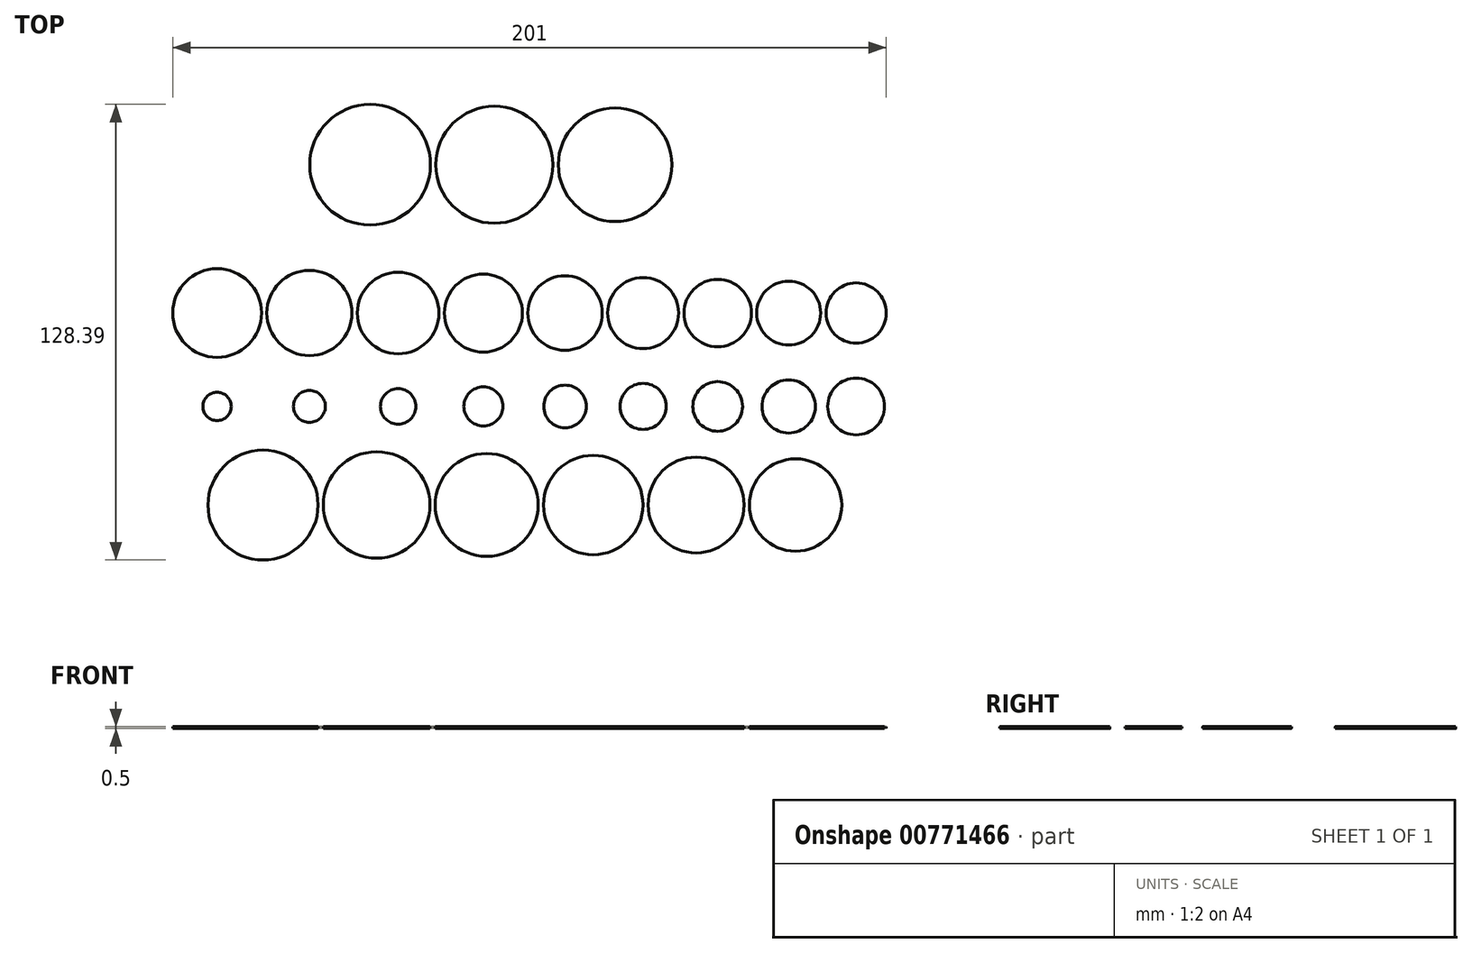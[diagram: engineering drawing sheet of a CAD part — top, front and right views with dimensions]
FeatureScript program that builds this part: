
annotation { "Feature Type Name" : "Feature", "Feature Type Description" : "" }
export const myFeature = defineFeature(function(context is Context, id is Id, definition is map)
    precondition{}
    {
        {
            var Q0;
            Q0=qCreatedBy(makeId("Top.planeOp"),FACE);
            var sketch = newSketch(context, id + "F0", { "sketchPlane" : qUnion([Q0])});
            skLineSegment(sketch, "E0", {"start": v(-97.7, 0) * mm, "end": v(119.62, 0) * mm, "construction": true});
            skCircle(sketch, "E1", {"center": v(-89.8, 0) * mm, "radius": 12.5 * mm});
            skCircle(sketch, "E2", {"center": v(-63.8, 0) * mm, "radius": 12 * mm});
            skCircle(sketch, "E3", {"center": v(-38.8, 0) * mm, "radius": 11.5 * mm});
            skCircle(sketch, "E4", {"center": v(-14.8, 0) * mm, "radius": 11 * mm});
            skCircle(sketch, "E5", {"center": v(8.2, 0) * mm, "radius": 10.5 * mm});
            skCircle(sketch, "E6", {"center": v(30.2, 0) * mm, "radius": 10 * mm});
            skCircle(sketch, "E7", {"center": v(51.2, 0) * mm, "radius": 9.5 * mm});
            skCircle(sketch, "E8", {"center": v(71.2, 0) * mm, "radius": 9 * mm});
            skCircle(sketch, "E9", {"center": v(90.2, 0) * mm, "radius": 8.5 * mm});
            skLineSegment(sketch, "E10", {"start": v(-97.7, -26.31) * mm, "end": v(119.62, -26.31) * mm, "construction": true});
            skCircle(sketch, "E11", {"center": v(-89.8, -26.31) * mm, "radius": 4 * mm});
            skCircle(sketch, "E12", {"center": v(-63.8, -26.31) * mm, "radius": 4.5 * mm});
            skCircle(sketch, "E13", {"center": v(-38.8, -26.31) * mm, "radius": 5 * mm});
            skCircle(sketch, "E14", {"center": v(-14.8, -26.31) * mm, "radius": 5.5 * mm});
            skCircle(sketch, "E15", {"center": v(8.2, -26.31) * mm, "radius": 6 * mm});
            skCircle(sketch, "E16", {"center": v(30.2, -26.31) * mm, "radius": 6.5 * mm});
            skCircle(sketch, "E17", {"center": v(51.2, -26.31) * mm, "radius": 7 * mm});
            skCircle(sketch, "E18", {"center": v(71.2, -26.31) * mm, "radius": 7.5 * mm});
            skCircle(sketch, "E19", {"center": v(90.2, -26.31) * mm, "radius": 8 * mm});
            skLineSegment(sketch, "E20", {"start": v(-97.7, -54.09) * mm, "end": v(120.28, -54.09) * mm, "construction": true});
            skCircle(sketch, "E21", {"center": v(-46.7, 41.8) * mm, "radius": 17 * mm});
            skCircle(sketch, "E22", {"center": v(-11.7, 41.8) * mm, "radius": 16.5 * mm});
            skCircle(sketch, "E23", {"center": v(22.3, 41.8) * mm, "radius": 16 * mm});
            skCircle(sketch, "E24", {"center": v(-76.87, -54.09) * mm, "radius": 15.5 * mm});
            skCircle(sketch, "E25", {"center": v(-44.87, -54.09) * mm, "radius": 15 * mm});
            skCircle(sketch, "E26", {"center": v(-13.87, -54.09) * mm, "radius": 14.5 * mm});
            skCircle(sketch, "E27", {"center": v(16.13, -54.09) * mm, "radius": 14 * mm});
            skCircle(sketch, "E28", {"center": v(45.13, -54.09) * mm, "radius": 13.5 * mm});
            skCircle(sketch, "E29", {"center": v(73.13, -54.09) * mm, "radius": 13 * mm});
            skLineSegment(sketch, "E30", {"start": v(-97.7, 41.8) * mm, "end": v(119.62, 41.8) * mm, "construction": true});
            skSolve(sketch);
        }
        {
            var Q0;
            Q0=makeQuery(id+"F0.imprint","IMPRINT",FACE,{"disambiguationData":[TD([[makeQuery(id+"F0.imprint","IMPRINT",EDGE,{"derivedFrom":sQuery(id+"F0.wireOp",EDGE,"E15")}),1.0]])]});
            var Q1;
            Q1=makeQuery(id+"F0.imprint","IMPRINT",FACE,{"disambiguationData":[TD([[makeQuery(id+"F0.imprint","IMPRINT",EDGE,{"derivedFrom":sQuery(id+"F0.wireOp",EDGE,"E18")}),1.0]])]});
            var Q2;
            Q2=makeQuery(id+"F0.imprint","IMPRINT",FACE,{"disambiguationData":[TD([[makeQuery(id+"F0.imprint","IMPRINT",EDGE,{"derivedFrom":sQuery(id+"F0.wireOp",EDGE,"E17")}),1.0]])]});
            var Q3;
            Q3=makeQuery(id+"F0.imprint","IMPRINT",FACE,{"disambiguationData":[TD([[makeQuery(id+"F0.imprint","IMPRINT",EDGE,{"derivedFrom":sQuery(id+"F0.wireOp",EDGE,"E16")}),1.0]])]});
            var Q4;
            Q4=makeQuery(id+"F0.imprint","IMPRINT",FACE,{"disambiguationData":[TD([[makeQuery(id+"F0.imprint","IMPRINT",EDGE,{"derivedFrom":sQuery(id+"F0.wireOp",EDGE,"E19")}),1.0]])]});
            var Q5;
            Q5=makeQuery(id+"F0.imprint","IMPRINT",FACE,{"disambiguationData":[TD([[makeQuery(id+"F0.imprint","IMPRINT",EDGE,{"derivedFrom":sQuery(id+"F0.wireOp",EDGE,"E1")}),1.0]])]});
            var Q6;
            Q6=makeQuery(id+"F0.imprint","IMPRINT",FACE,{"disambiguationData":[TD([[makeQuery(id+"F0.imprint","IMPRINT",EDGE,{"derivedFrom":sQuery(id+"F0.wireOp",EDGE,"E2")}),1.0]])]});
            var Q7;
            Q7=makeQuery(id+"F0.imprint","IMPRINT",FACE,{"disambiguationData":[TD([[makeQuery(id+"F0.imprint","IMPRINT",EDGE,{"derivedFrom":sQuery(id+"F0.wireOp",EDGE,"E3")}),1.0]])]});
            var Q8;
            Q8=makeQuery(id+"F0.imprint","IMPRINT",FACE,{"disambiguationData":[TD([[makeQuery(id+"F0.imprint","IMPRINT",EDGE,{"derivedFrom":sQuery(id+"F0.wireOp",EDGE,"E4")}),1.0]])]});
            var Q9;
            Q9=makeQuery(id+"F0.imprint","IMPRINT",FACE,{"disambiguationData":[TD([[makeQuery(id+"F0.imprint","IMPRINT",EDGE,{"derivedFrom":sQuery(id+"F0.wireOp",EDGE,"E5")}),1.0]])]});
            var Q10;
            Q10=makeQuery(id+"F0.imprint","IMPRINT",FACE,{"disambiguationData":[TD([[makeQuery(id+"F0.imprint","IMPRINT",EDGE,{"derivedFrom":sQuery(id+"F0.wireOp",EDGE,"E6")}),1.0]])]});
            var Q11;
            Q11=makeQuery(id+"F0.imprint","IMPRINT",FACE,{"disambiguationData":[TD([[makeQuery(id+"F0.imprint","IMPRINT",EDGE,{"derivedFrom":sQuery(id+"F0.wireOp",EDGE,"E8")}),1.0]])]});
            var Q12;
            Q12=makeQuery(id+"F0.imprint","IMPRINT",FACE,{"disambiguationData":[TD([[makeQuery(id+"F0.imprint","IMPRINT",EDGE,{"derivedFrom":sQuery(id+"F0.wireOp",EDGE,"E7")}),1.0]])]});
            var Q13;
            Q13=makeQuery(id+"F0.imprint","IMPRINT",FACE,{"disambiguationData":[TD([[makeQuery(id+"F0.imprint","IMPRINT",EDGE,{"derivedFrom":sQuery(id+"F0.wireOp",EDGE,"E9")}),1.0]])]});
            var Q14;
            Q14=makeQuery(id+"F0.imprint","IMPRINT",FACE,{"disambiguationData":[TD([[makeQuery(id+"F0.imprint","IMPRINT",EDGE,{"derivedFrom":sQuery(id+"F0.wireOp",EDGE,"E11")}),1.0]])]});
            var Q15;
            Q15=makeQuery(id+"F0.imprint","IMPRINT",FACE,{"disambiguationData":[TD([[makeQuery(id+"F0.imprint","IMPRINT",EDGE,{"derivedFrom":sQuery(id+"F0.wireOp",EDGE,"E12")}),1.0]])]});
            var Q16;
            Q16=makeQuery(id+"F0.imprint","IMPRINT",FACE,{"disambiguationData":[TD([[makeQuery(id+"F0.imprint","IMPRINT",EDGE,{"derivedFrom":sQuery(id+"F0.wireOp",EDGE,"E13")}),1.0]])]});
            var Q17;
            Q17=makeQuery(id+"F0.imprint","IMPRINT",FACE,{"disambiguationData":[TD([[makeQuery(id+"F0.imprint","IMPRINT",EDGE,{"derivedFrom":sQuery(id+"F0.wireOp",EDGE,"E14")}),1.0]])]});
            var Q18;
            Q18=makeQuery(id+"F0.imprint","IMPRINT",FACE,{"disambiguationData":[TD([[makeQuery(id+"F0.imprint","IMPRINT",EDGE,{"derivedFrom":sQuery(id+"F0.wireOp",EDGE,"E21")}),1.0]])]});
            var Q19;
            Q19=makeQuery(id+"F0.imprint","IMPRINT",FACE,{"disambiguationData":[TD([[makeQuery(id+"F0.imprint","IMPRINT",EDGE,{"derivedFrom":sQuery(id+"F0.wireOp",EDGE,"E22")}),1.0]])]});
            var Q20;
            Q20=makeQuery(id+"F0.imprint","IMPRINT",FACE,{"disambiguationData":[TD([[makeQuery(id+"F0.imprint","IMPRINT",EDGE,{"derivedFrom":sQuery(id+"F0.wireOp",EDGE,"E23")}),1.0]])]});
            var Q21;
            Q21=makeQuery(id+"F0.imprint","IMPRINT",FACE,{"disambiguationData":[TD([[makeQuery(id+"F0.imprint","IMPRINT",EDGE,{"derivedFrom":sQuery(id+"F0.wireOp",EDGE,"E24")}),1.0]])]});
            var Q22;
            Q22=makeQuery(id+"F0.imprint","IMPRINT",FACE,{"disambiguationData":[TD([[makeQuery(id+"F0.imprint","IMPRINT",EDGE,{"derivedFrom":sQuery(id+"F0.wireOp",EDGE,"E25")}),1.0]])]});
            var Q23;
            Q23=makeQuery(id+"F0.imprint","IMPRINT",FACE,{"disambiguationData":[TD([[makeQuery(id+"F0.imprint","IMPRINT",EDGE,{"derivedFrom":sQuery(id+"F0.wireOp",EDGE,"E26")}),1.0]])]});
            var Q24;
            Q24=makeQuery(id+"F0.imprint","IMPRINT",FACE,{"disambiguationData":[TD([[makeQuery(id+"F0.imprint","IMPRINT",EDGE,{"derivedFrom":sQuery(id+"F0.wireOp",EDGE,"E27")}),1.0]])]});
            var Q25;
            Q25=makeQuery(id+"F0.imprint","IMPRINT",FACE,{"disambiguationData":[TD([[makeQuery(id+"F0.imprint","IMPRINT",EDGE,{"derivedFrom":sQuery(id+"F0.wireOp",EDGE,"E29")}),1.0]])]});
            var Q26;
            Q26=makeQuery(id+"F0.imprint","IMPRINT",FACE,{"disambiguationData":[TD([[makeQuery(id+"F0.imprint","IMPRINT",EDGE,{"derivedFrom":sQuery(id+"F0.wireOp",EDGE,"E28")}),1.0]])]});
            extrude(context, id + "F1", {"entities" : qUnion([Q0, Q1, Q2, Q3, Q4, Q5, Q6, Q7, Q8, Q9, Q10, Q11, Q12, Q13, Q14, Q15, Q16, Q17, Q18, Q19, Q20, Q21, Q22, Q23, Q24, Q25, Q26]), "depth" : 0.5 * mm, "offsetDistance" : 25 * mm});
        }
    });
